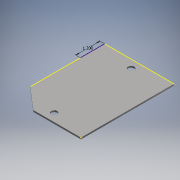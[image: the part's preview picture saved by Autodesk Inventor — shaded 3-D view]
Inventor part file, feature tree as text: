
AUTODESK INVENTOR PART (.ipt)
format: ipt  version: 2017 (Build 210142000, 142)  size: 115,200 bytes
history: native  units: in
note: dims shown in document units (in); Inventor stores cm internally (conversion verified against a paired STEP export)
features: sketch x3, other x3, extrude x2, reference x1
ambient origin geometry x8: Origin, YZ Plane, XZ Plane, XY Plane, X Axis, Y Axis, Z Axis, Center Point
bodies: Body1 (feature_tree)
feature tree (9):
  extrude  "Extrusion3"  Depth=3.45in
  sketch  "Sketch2"  dims[d2=3.68in d3=2.36in]
  extrude  "Extrusion4"  Depth=2.36in
  sketch  "Sketch1"  dims[d0=4.61in d1=3.45in]
  sketch  "Sketch3"  dims[d10=0.3in d17=0.077in d18=0.0in d19=1.2in d20=1.0in d21=0.0in]
  reference  "Reference1"
  other  "Assembly1"
  other  "Flywheel w motor:1"
  other  "am-2875+Banebots+P60+4-1:1"
